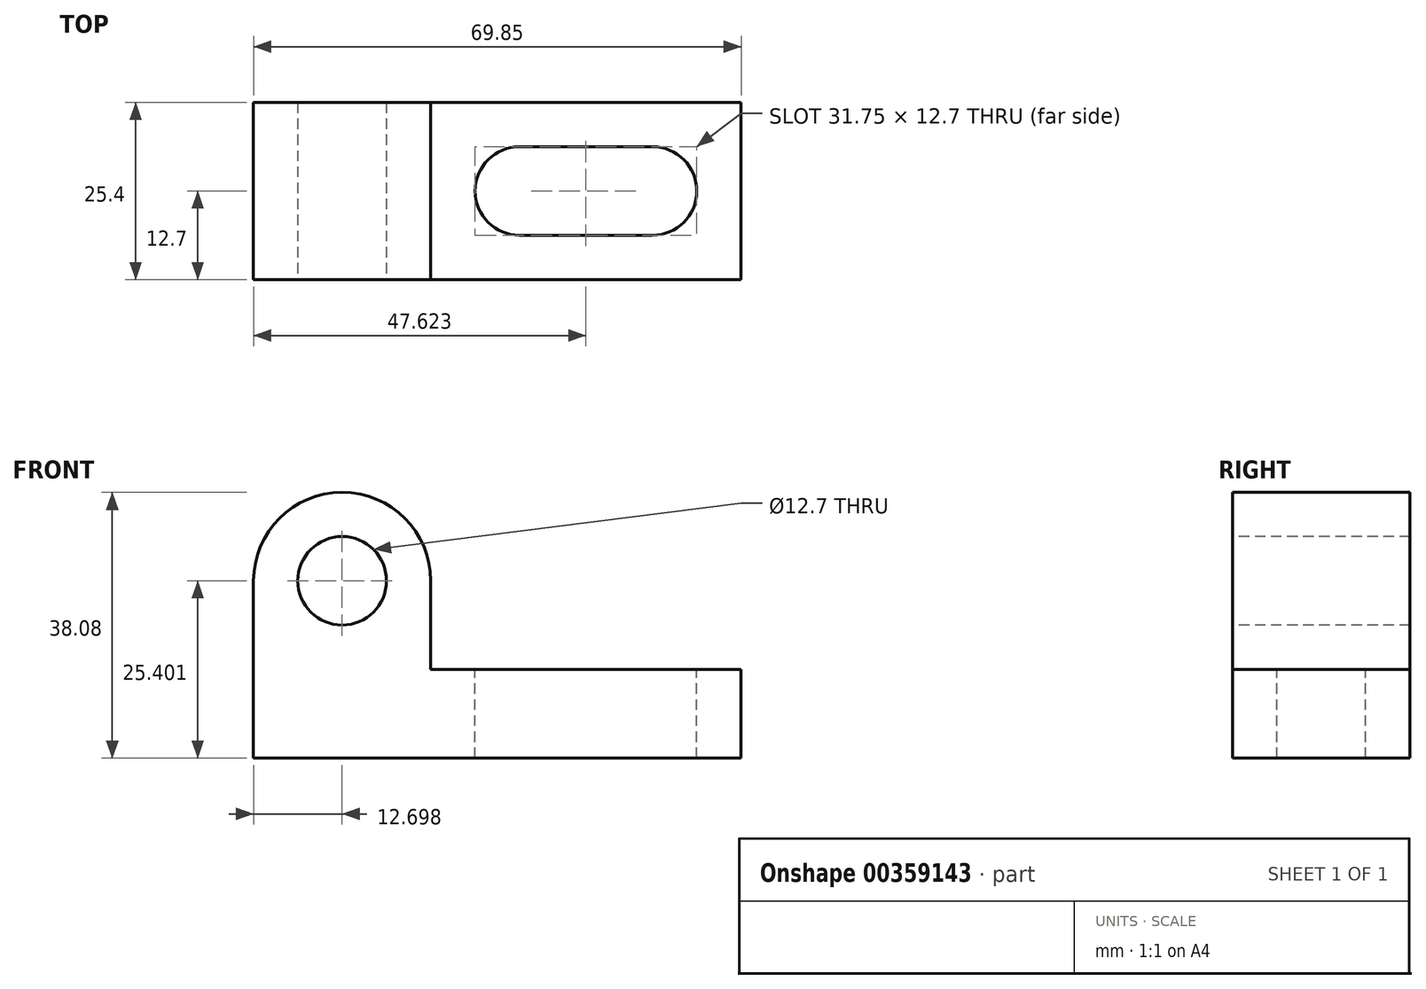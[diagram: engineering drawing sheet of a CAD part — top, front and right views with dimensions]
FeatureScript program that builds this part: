
annotation { "Feature Type Name" : "Feature", "Feature Type Description" : "" }
export const myFeature = defineFeature(function(context is Context, id is Id, definition is map)
    precondition{}
    {
        {
            var Q0;
            Q0=qCreatedBy(makeId("Front.planeOp"),FACE);
            var sketch = newSketch(context, id + "F0", { "sketchPlane" : qUnion([Q0])});
            skLineSegment(sketch, "E0", {"start": v(-71.82, 20.12) * mm, "end": v(-46.42, 20.12) * mm});
            skLineSegment(sketch, "E1", {"start": v(-46.42, 20.12) * mm, "end": v(-46.42, -5.28) * mm});
            skLineSegment(sketch, "E2", {"start": v(-46.42, -5.28) * mm, "end": v(-1.97, -5.28) * mm});
            skLineSegment(sketch, "E3", {"start": v(-1.97, -5.28) * mm, "end": v(-1.97, -17.98) * mm});
            skLineSegment(sketch, "E4", {"start": v(-1.97, -17.98) * mm, "end": v(-71.82, -17.98) * mm});
            skLineSegment(sketch, "E5", {"start": v(-71.82, -17.98) * mm, "end": v(-71.82, 20.12) * mm});
            skSolve(sketch);
        }
        {
            var Q0;
            Q0 = qSketchRegion(id + "F0", true);
            extrude(context, id + "F1", {"entities" : qUnion([Q0]), "depth" : 25.4 * mm});
        }
        {
            var Q0;
            Q0=makeQuery(id+"F1.opExtrude","CAP_FACE",FACE,{"disambiguationData":[OSD([sQuery(id+"F0.wireOp",EDGE,"E0"),sQuery(id+"F0.wireOp",EDGE,"E1"),sQuery(id+"F0.wireOp",EDGE,"E2"),sQuery(id+"F0.wireOp",EDGE,"E3"),sQuery(id+"F0.wireOp",EDGE,"E4"),sQuery(id+"F0.wireOp",EDGE,"E5")])],"isStart":false});
            var sketch = newSketch(context, id + "F2", { "sketchPlane" : qUnion([Q0])});
            skCircle(sketch, "E6", {"center": v(-59.12, 7.42) * mm, "radius": 6.35 * mm});
            skArc(sketch, "E7", {"start": v(-46.42, 7.42) * mm, "mid": v(-59.12, 20.1) * mm, "end": v(-71.82, 7.42) * mm});
            skSolve(sketch);
        }
        {
            var Q0;
            Q0=makeQuery(id+"F1.opExtrude","SWEPT_FACE",FACE,{"disambiguationData":[OSD([sQuery(id+"F0.wireOp",EDGE,"E2")])]});
            var sketch = newSketch(context, id + "F3", { "sketchPlane" : qUnion([Q0])});
            skCircle(sketch, "E8", {"center": v(-33.72, -12.7) * mm, "radius": 6.35 * mm});
            skCircle(sketch, "E9", {"center": v(-14.67, -12.7) * mm, "radius": 6.35 * mm});
            skLineSegment(sketch, "E10", {"start": v(-33.72, -19.05) * mm, "end": v(-14.67, -19.05) * mm});
            skLineSegment(sketch, "E11", {"start": v(-33.72, -6.35) * mm, "end": v(-14.67, -6.35) * mm});
            skSolve(sketch);
        }
        {
            var Q0;
            {var subQ0=sQuery(id+"F3.wireOp",EDGE,"E9");var subQ1=makeQuery(id+"F3.imprint","INTERSECT",VERTEX,{"derivedFrom":[subQ0,sQuery(id+"F3.wireOp",EDGE,"E10")]});Q0=makeQuery(id+"F3.imprint","IMPRINT",FACE,{"disambiguationData":[TD([[makeQuery(id+"F3.imprint","IMPRINT",EDGE,{"disambiguationData":[TD([[subQ1,1.0]])],"derivedFrom":subQ0}),1.0]])]});}
            var Q1;
            {var subQ0=sQuery(id+"F3.wireOp",EDGE,"E10");Q1=makeQuery(id+"F3.imprint","IMPRINT",FACE,{"disambiguationData":[TD([[makeQuery(id+"F3.imprint","IMPRINT",EDGE,{"derivedFrom":subQ0}),1.0]])]});}
            var Q2;
            {var subQ0=sQuery(id+"F3.wireOp",EDGE,"E8");var subQ1=makeQuery(id+"F3.imprint","INTERSECT",VERTEX,{"derivedFrom":[subQ0,sQuery(id+"F3.wireOp",EDGE,"E10")]});Q2=makeQuery(id+"F3.imprint","IMPRINT",FACE,{"disambiguationData":[TD([[makeQuery(id+"F3.imprint","IMPRINT",EDGE,{"disambiguationData":[TD([[subQ1,1.0]])],"derivedFrom":subQ0}),1.0]])]});}
            extrude(context, id + "F4", {"entities" : qUnion([Q0, Q1, Q2]), "operationType" : NewBodyOperationType.REMOVE, "oppositeDirection" : true, "depth" : 12.7 * mm});
        }
        {
            var Q0;
            Q0=makeQuery(id+"F2.imprint","IMPRINT",FACE,{"disambiguationData":[TD([[makeQuery(id+"F2.imprint","IMPRINT",EDGE,{"derivedFrom":sQuery(id+"F2.wireOp",EDGE,"E6")}),1.0]])]});
            var Q1;
            {var subQ0=sQuery(id+"F2.wireOp",EDGE,"E7");Q1=makeQuery(id+"F2.imprint","IMPRINT",FACE,{"disambiguationData":[TD([[makeQuery(id+"F2.imprint","IMPRINT",EDGE,{"derivedFrom":subQ0}),-1.0]])]});}
            extrude(context, id + "F5", {"entities" : qUnion([Q0, Q1]), "operationType" : NewBodyOperationType.REMOVE, "oppositeDirection" : true, "depth" : 25.4 * mm});
        }
    });
